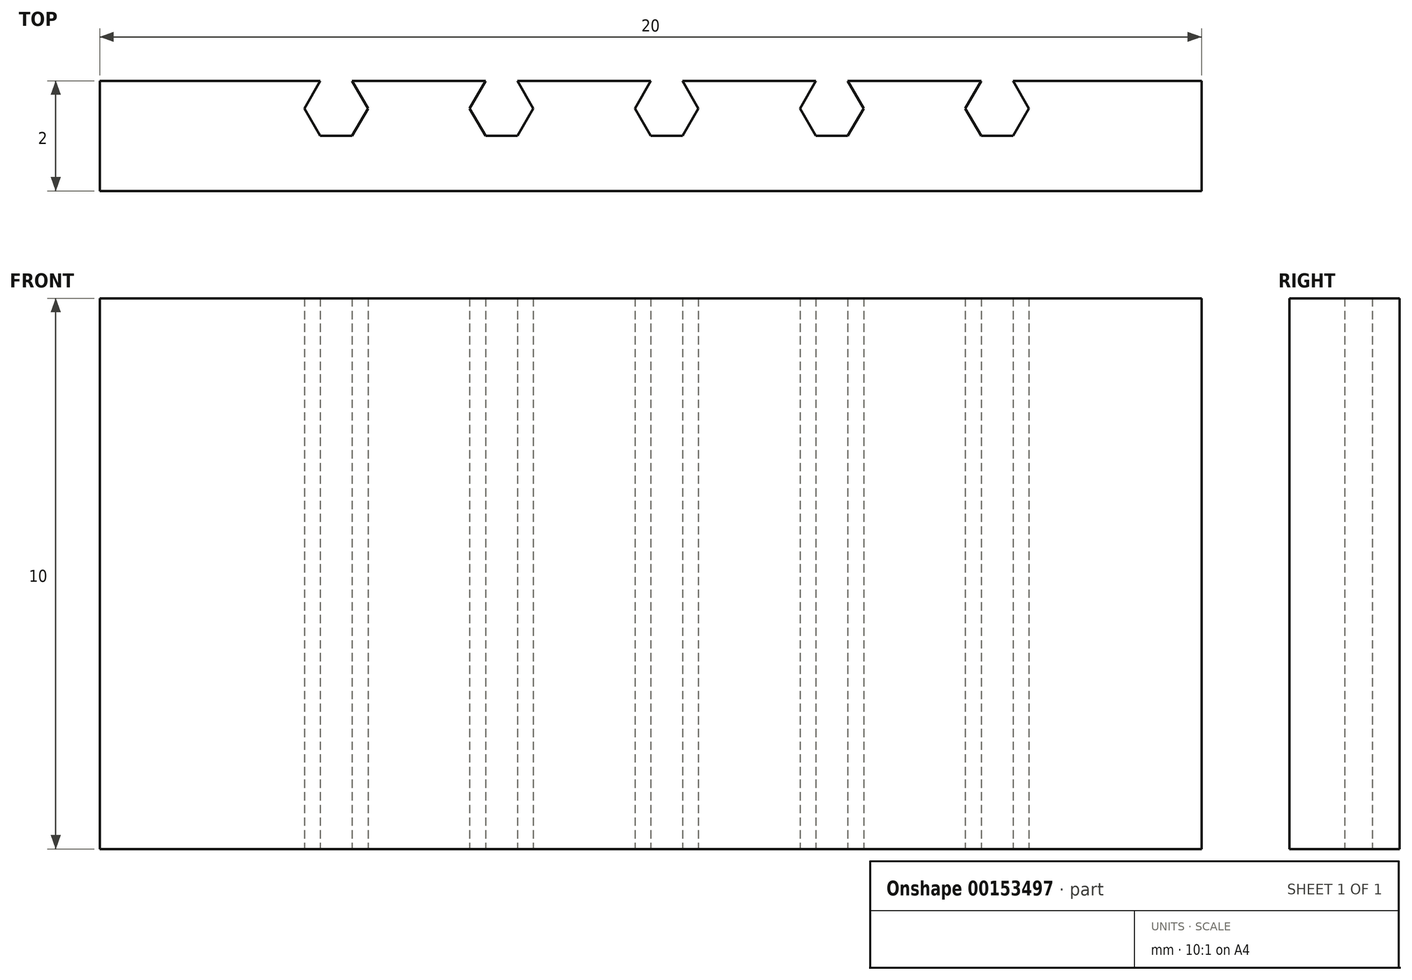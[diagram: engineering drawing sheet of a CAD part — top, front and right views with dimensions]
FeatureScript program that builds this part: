
annotation { "Feature Type Name" : "Feature", "Feature Type Description" : "" }
export const myFeature = defineFeature(function(context is Context, id is Id, definition is map)
    precondition{}
    {
        {
            var Q0;
            Q0=qCreatedBy(makeId("Top.planeOp"),FACE);
            var sketch = newSketch(context, id + "F0", { "sketchPlane" : qUnion([Q0])});
            skLineSegment(sketch, "E0.top", {"start": v(7.21, -3) * mm, "end": v(-12.79, -3) * mm});
            skPoint(sketch, "E0.middle", {"position": v(0, 0) * mm});
            skCircle(sketch, "E1.cCircle", {"center": v(-8.5, -1.5) * mm, "radius": 0.5 * mm, "construction": true});
            skLineSegment(sketch, "E1.1", {"start": v(-8.21, -1) * mm, "end": v(-7.92, -1.5) * mm});
            skLineSegment(sketch, "E1.2", {"start": v(-7.92, -1.5) * mm, "end": v(-8.21, -2) * mm});
            skLineSegment(sketch, "E1.3", {"start": v(-8.21, -2) * mm, "end": v(-8.79, -2) * mm});
            skLineSegment(sketch, "E1.4", {"start": v(-8.79, -2) * mm, "end": v(-9.08, -1.5) * mm});
            skLineSegment(sketch, "E1.5", {"start": v(-9.08, -1.5) * mm, "end": v(-8.79, -1) * mm});
            skPoint(sketch, "E1.0.midPoint", {"position": v(-8.5, -1) * mm});
            skLineSegment(sketch, "E2", {"start": v(-8.21, -1) * mm, "end": v(-5.79, -1) * mm});
            skLineSegment(sketch, "E3", {"start": v(-8.79, -1) * mm, "end": v(-12.79, -1) * mm});
            skLineSegment(sketch, "E4", {"start": v(-12.79, -1) * mm, "end": v(-12.79, -3) * mm});
            skLineSegment(sketch, "E5", {"start": v(7.21, -1) * mm, "end": v(7.21, -3) * mm});
            skLineSegment(sketch, "E6.1.0.0", {"start": v(-4.92, -1.5) * mm, "end": v(-5.21, -2) * mm});
            skCircle(sketch, "E6.1.0.1", {"center": v(-5.5, -1.5) * mm, "radius": 0.5 * mm, "construction": true});
            skPoint(sketch, "E6.1.0.2", {"position": v(-5.5, -1) * mm});
            skLineSegment(sketch, "E6.1.0.3", {"start": v(-5.21, -1) * mm, "end": v(-4.92, -1.5) * mm});
            skLineSegment(sketch, "E6.1.0.4", {"start": v(-5.21, -2) * mm, "end": v(-5.79, -2) * mm});
            skLineSegment(sketch, "E6.1.0.5", {"start": v(-6.08, -1.5) * mm, "end": v(-5.79, -1) * mm});
            skLineSegment(sketch, "E6.1.0.6", {"start": v(-5.79, -2) * mm, "end": v(-6.08, -1.5) * mm});
            skLineSegment(sketch, "E6.2.0.0", {"start": v(-1.92, -1.5) * mm, "end": v(-2.21, -2) * mm});
            skCircle(sketch, "E6.2.0.1", {"center": v(-2.5, -1.5) * mm, "radius": 0.5 * mm, "construction": true});
            skPoint(sketch, "E6.2.0.2", {"position": v(-2.5, -1) * mm});
            skLineSegment(sketch, "E6.2.0.3", {"start": v(-2.21, -1) * mm, "end": v(-1.92, -1.5) * mm});
            skLineSegment(sketch, "E6.2.0.4", {"start": v(-2.21, -2) * mm, "end": v(-2.79, -2) * mm});
            skLineSegment(sketch, "E6.2.0.5", {"start": v(-3.08, -1.5) * mm, "end": v(-2.79, -1) * mm});
            skLineSegment(sketch, "E6.2.0.6", {"start": v(-2.79, -2) * mm, "end": v(-3.08, -1.5) * mm});
            skLineSegment(sketch, "E6.3.0.0", {"start": v(1.08, -1.5) * mm, "end": v(0.79, -2) * mm});
            skCircle(sketch, "E6.3.0.1", {"center": v(0.5, -1.5) * mm, "radius": 0.5 * mm, "construction": true});
            skPoint(sketch, "E6.3.0.2", {"position": v(0.5, -1) * mm});
            skLineSegment(sketch, "E6.3.0.3", {"start": v(0.79, -1) * mm, "end": v(1.08, -1.5) * mm});
            skLineSegment(sketch, "E6.3.0.4", {"start": v(0.79, -2) * mm, "end": v(0.21, -2) * mm});
            skLineSegment(sketch, "E6.3.0.5", {"start": v(-0.08, -1.5) * mm, "end": v(0.21, -1) * mm});
            skLineSegment(sketch, "E6.3.0.6", {"start": v(0.21, -2) * mm, "end": v(-0.08, -1.5) * mm});
            skLineSegment(sketch, "E6.4.0.0", {"start": v(4.08, -1.5) * mm, "end": v(3.79, -2) * mm});
            skCircle(sketch, "E6.4.0.1", {"center": v(3.5, -1.5) * mm, "radius": 0.5 * mm, "construction": true});
            skPoint(sketch, "E6.4.0.2", {"position": v(3.5, -1) * mm});
            skLineSegment(sketch, "E6.4.0.3", {"start": v(3.79, -1) * mm, "end": v(4.08, -1.5) * mm});
            skLineSegment(sketch, "E6.4.0.4", {"start": v(3.79, -2) * mm, "end": v(3.21, -2) * mm});
            skLineSegment(sketch, "E6.4.0.5", {"start": v(2.92, -1.5) * mm, "end": v(3.21, -1) * mm});
            skLineSegment(sketch, "E6.4.0.6", {"start": v(3.21, -2) * mm, "end": v(2.92, -1.5) * mm});
            skLineSegment(sketch, "E6.direction1", {"start": v(-8.79, -2) * mm, "end": v(-5.79, -2) * mm, "construction": true});
            skLineSegment(sketch, "E7.trimOffspring", {"start": v(-5.21, -1) * mm, "end": v(-2.79, -1) * mm});
            skLineSegment(sketch, "E8.trimOffspring", {"start": v(-2.21, -1) * mm, "end": v(0.21, -1) * mm});
            skLineSegment(sketch, "E9.trimOffspring", {"start": v(0.79, -1) * mm, "end": v(3.21, -1) * mm});
            skLineSegment(sketch, "E10.trimOffspring", {"start": v(3.79, -1) * mm, "end": v(7.21, -1) * mm});
            skSolve(sketch);
        }
        {
            var Q0;
            Q0=makeQuery(id+"F0.imprint","IMPRINT",FACE,{"disambiguationData":[TD([[makeQuery(id+"F0.imprint","IMPRINT",EDGE,{"derivedFrom":sQuery(id+"F0.wireOp",EDGE,"E0.top")}),-1.0]])]});
            extrude(context, id + "F1", {"entities" : qUnion([Q0]), "depth" : 10 * mm});
        }
    });
